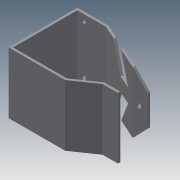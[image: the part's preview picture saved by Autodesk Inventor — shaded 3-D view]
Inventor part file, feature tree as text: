
AUTODESK INVENTOR PART (.ipt)
format: ipt  version: 2013 (Build 170138000, 138)  size: 218,624 bytes
history: native  units: mm
features: sketch x17, extrude x13
ambient origin geometry x8: Origin, YZ Plane, XZ Plane, XY Plane, X Axis, Y Axis, Z Axis, Center Point
bodies: Solid1 (feature_tree)
feature tree (30):
  extrude  "Extrusion1"  Depth=40.0mm
  extrude  "Extrusion2"  Depth=22.0mm
  extrude  "Extrusion3"  Depth=8.0mm
  sketch  "Sketch4"  dims[d7=10.0mm d12=1.5mm]
  sketch  "Sketch5"  dims[d13=40.0mm d14=0.0mm d15=10.0mm]
  sketch  "Sketch6"  dims[d16=18.0mm d17=60.0deg]
  sketch  "Sketch7"  dims[d18=10.0mm d21=18.0mm]
  extrude  "Extrusion4"  Depth=1.5mm
  extrude  "Extrusion5"  Depth=10.0mm
  extrude  "Extrusion6"  TaperAngle=60.0deg  [1 undecoded]
  extrude  "Extrusion7"  Depth=18.0mm
  extrude  "Extrusion8"  Depth=10.0mm
  extrude  "Extrusion9"  Depth=3.0mm
  sketch  "Sketch13"  dims[d39=3.0mm d40=1.5mm d41=0.0mm]
  sketch  "Sketch14"  dims[d42=1.5mm d43=0.0mm]
  extrude  "Extrusion10"  Depth=10.0mm
  extrude  "Extrusion11"  Depth=3.0mm
  extrude  "Extrusion12"  Depth=3.0mm
  extrude  "Extrusion13"  Depth=1.5mm TaperAngle=0.0deg
  sketch  "Sketch1"  dims[d0=19.0mm d1=40.0mm]
  sketch  "Sketch2"  dims[d2=1.5mm d3=0.0mm d4=22.0mm]
  sketch  "Sketch3"  dims[d5=60.0mm d6=8.0mm]
  sketch  "Sketch8"  dims[d22=60.0deg d23=10.0mm]
  sketch  "Sketch9"  dims[d24=1.5mm d25=0.0mm d26=3.0mm]
  sketch  "Sketch10"  dims[d27=10.0mm d28=10.0mm]
  sketch  "Sketch11"  dims[d29=1.5mm d30=0.0mm d31=3.0mm]
  sketch  "Sketch12"  dims[d32=1.5mm d33=0.0mm d38=3.0mm]
  sketch  "Sketch15"  dims[d44=6.0mm]
  sketch  "Sketch16"  dims[d45=3.0mm]
  sketch  "Sketch17"  dims[d46=1.5mm d47=0.0mm d48=1.5mm d49=38.0mm d50=0.0mm d51=1.5mm d52=1.5mm d53=0.0mm d54=4.0mm d55=0.0mm d56=1.5mm d57=1.5mm d58=37.0mm d59=0.0mm d60=18.0mm d61=60.0mm d62=8.0mm d63=10.0mm d64=1.5mm d66=40.0mm d67=0.0mm]
note: 1 required parameter value undecoded (feature->parameter linkage not recoverable at this tier; creation-order binding heuristic only, values carry confidence <= 0.55)
